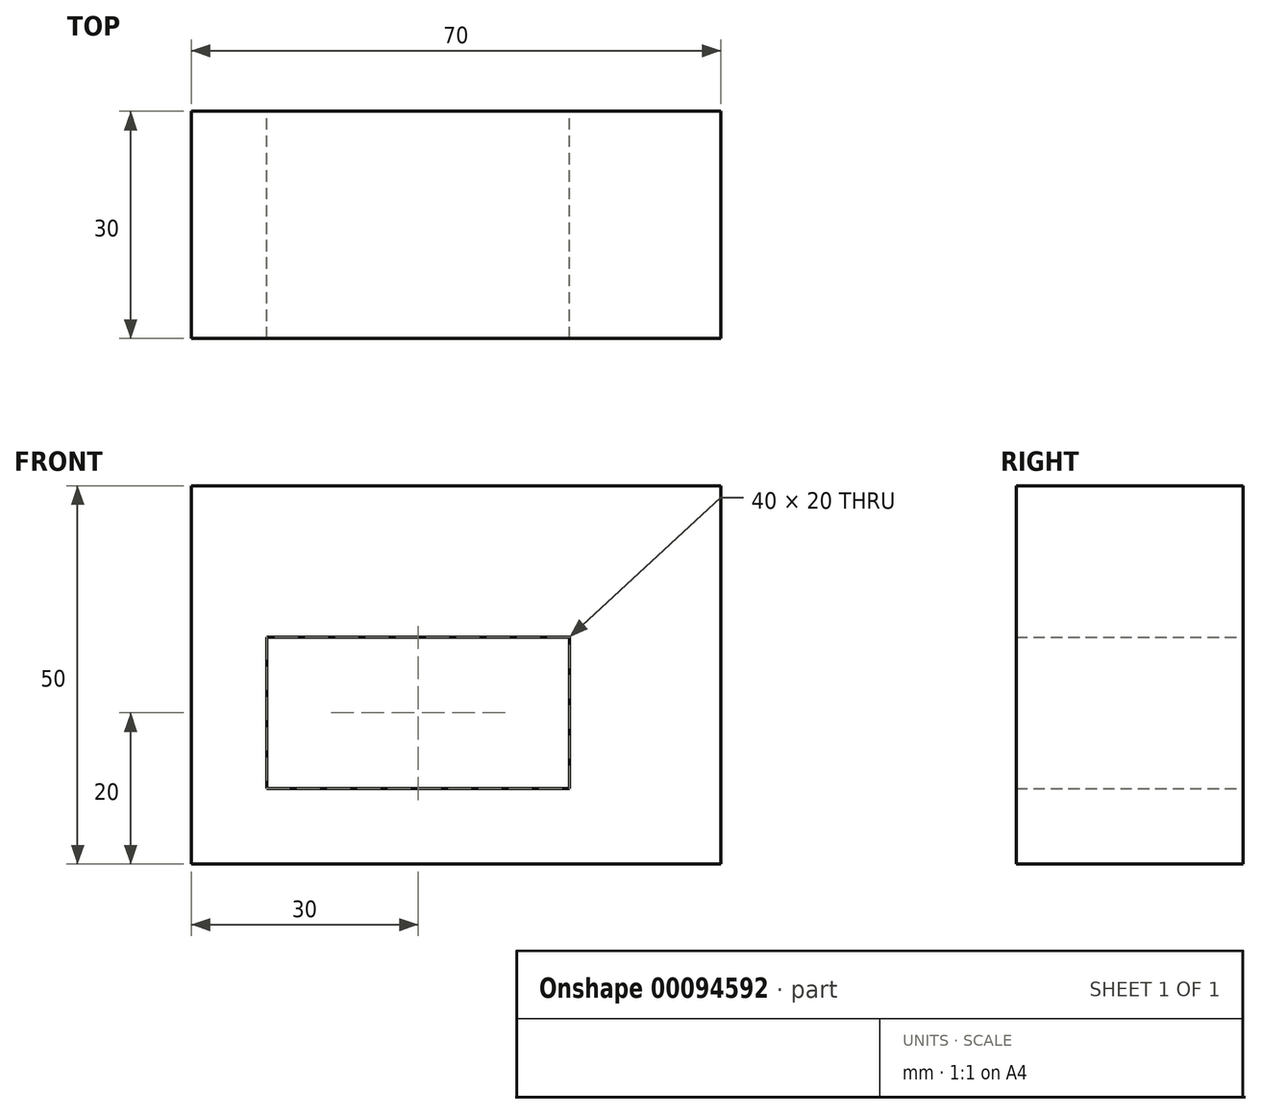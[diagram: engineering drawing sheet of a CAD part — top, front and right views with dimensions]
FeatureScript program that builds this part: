
annotation { "Feature Type Name" : "Feature", "Feature Type Description" : "" }
export const myFeature = defineFeature(function(context is Context, id is Id, definition is map)
    precondition{}
    {
        {
            var Q0;
            Q0=qCreatedBy(makeId("Front.planeOp"),FACE);
            var sketch = newSketch(context, id + "F0", { "sketchPlane" : qUnion([Q0])});
            skLineSegment(sketch, "E0", {"start": v(0, 50) * mm, "end": v(70, 50) * mm});
            skLineSegment(sketch, "E1", {"start": v(0, 50) * mm, "end": v(0, 0) * mm});
            skLineSegment(sketch, "E2", {"start": v(0, 0) * mm, "end": v(70, 0) * mm});
            skLineSegment(sketch, "E3", {"start": v(70, 50) * mm, "end": v(70, 0) * mm});
            skPoint(sketch, "E4.firstSnap0", {"position": v(0, 30) * mm});
            skLineSegment(sketch, "E4.bottom", {"start": v(10, 30) * mm, "end": v(50, 30) * mm});
            skLineSegment(sketch, "E4.top", {"start": v(10, 10) * mm, "end": v(50, 10) * mm});
            skLineSegment(sketch, "E4.left", {"start": v(10, 30) * mm, "end": v(10, 10) * mm});
            skLineSegment(sketch, "E4.right", {"start": v(50, 30) * mm, "end": v(50, 10) * mm});
            skSolve(sketch);
        }
        {
            var Q0;
            Q0=makeQuery(id+"F0.imprint","IMPRINT",FACE,{"disambiguationData":[TD([[makeQuery(id+"F0.imprint","IMPRINT",EDGE,{"derivedFrom":sQuery(id+"F0.wireOp",EDGE,"E0")}),-1.0]])]});
            var sketch = newSketch(context, id + "F1", { "sketchPlane" : qUnion([Q0])});
            skSolve(sketch);
        }
        {
            var Q0;
            Q0 = qSketchRegion(id + "F1", true);
            var Q1;
            Q1=makeQuery(id+"F0.imprint","IMPRINT",FACE,{"disambiguationData":[TD([[makeQuery(id+"F0.imprint","IMPRINT",EDGE,{"derivedFrom":sQuery(id+"F0.wireOp",EDGE,"E0")}),-1.0]])]});
            extrude(context, id + "F2", {"entities" : qUnion([Q0, Q1]), "depth" : 10 * mm});
        }
        {
            var Q0;
            Q0=makeQuery(id+"F1.imprint","IMPRINT",FACE,{"disambiguationData":[TD([[makeQuery(id+"F1.imprint","IMPRINT",EDGE,{"derivedFrom":makeQuery(id+"F0.imprint","IMPRINT",EDGE,{"derivedFrom":sQuery(id+"F0.wireOp",EDGE,"E0")})}),-1.0]])]});
            var Q1;
            Q1=makeQuery(id+"F2.opExtrude","CAP_FACE",FACE,{"disambiguationData":[OSD([sQuery(id+"F0.wireOp",EDGE,"E0"),sQuery(id+"F0.wireOp",EDGE,"E1"),sQuery(id+"F0.wireOp",EDGE,"E2"),sQuery(id+"F0.wireOp",EDGE,"E3"),sQuery(id+"F0.wireOp",EDGE,"E4.bottom"),sQuery(id+"F0.wireOp",EDGE,"E4.top"),sQuery(id+"F0.wireOp",EDGE,"E4.left"),sQuery(id+"F0.wireOp",EDGE,"E4.right")])],"isStart":false});
            extrude(context, id + "F3", {"entities" : qUnion([Q0, Q1]), "operationType" : NewBodyOperationType.ADD, "depth" : 10 * mm});
        }
        {
            var Q0;
            Q0=makeQuery(id+"F2.opExtrude","CAP_FACE",FACE,{"disambiguationData":[OSD([sQuery(id+"F0.wireOp",EDGE,"E0"),sQuery(id+"F0.wireOp",EDGE,"E1"),sQuery(id+"F0.wireOp",EDGE,"E2"),sQuery(id+"F0.wireOp",EDGE,"E3"),sQuery(id+"F0.wireOp",EDGE,"E4.bottom"),sQuery(id+"F0.wireOp",EDGE,"E4.top"),sQuery(id+"F0.wireOp",EDGE,"E4.left"),sQuery(id+"F0.wireOp",EDGE,"E4.right")])],"isStart":true});
            var Q1;
            {var subQ0=sQuery(id+"F0.wireOp",EDGE,"E4.right");var subQ1=sQuery(id+"F0.wireOp",EDGE,"E4.left");var subQ2=sQuery(id+"F0.wireOp",EDGE,"E4.top");var subQ3=sQuery(id+"F0.wireOp",EDGE,"E4.bottom");var subQ4=sQuery(id+"F0.wireOp",EDGE,"E3");var subQ5=sQuery(id+"F0.wireOp",EDGE,"E2");var subQ6=sQuery(id+"F0.wireOp",EDGE,"E1");var subQ7=sQuery(id+"F0.wireOp",EDGE,"E0");Q1=makeQuery(id+"F3.opExtrude","CAP_FACE",FACE,{"disambiguationData":[OSD([subQ7,subQ6,subQ5,subQ4,subQ3,subQ2,subQ1,subQ0]),TDD([makeQuery(id+"F2.opExtrude","CAP_FACE",FACE,{"disambiguationData":[OSD([subQ7,subQ6,subQ5,subQ4,subQ3,subQ2,subQ1,subQ0])],"isStart":false})])],"isStart":false});}
            extrude(context, id + "F4", {"entities" : qUnion([Q0, Q1]), "operationType" : NewBodyOperationType.ADD, "depth" : 10 * mm});
        }
    });
